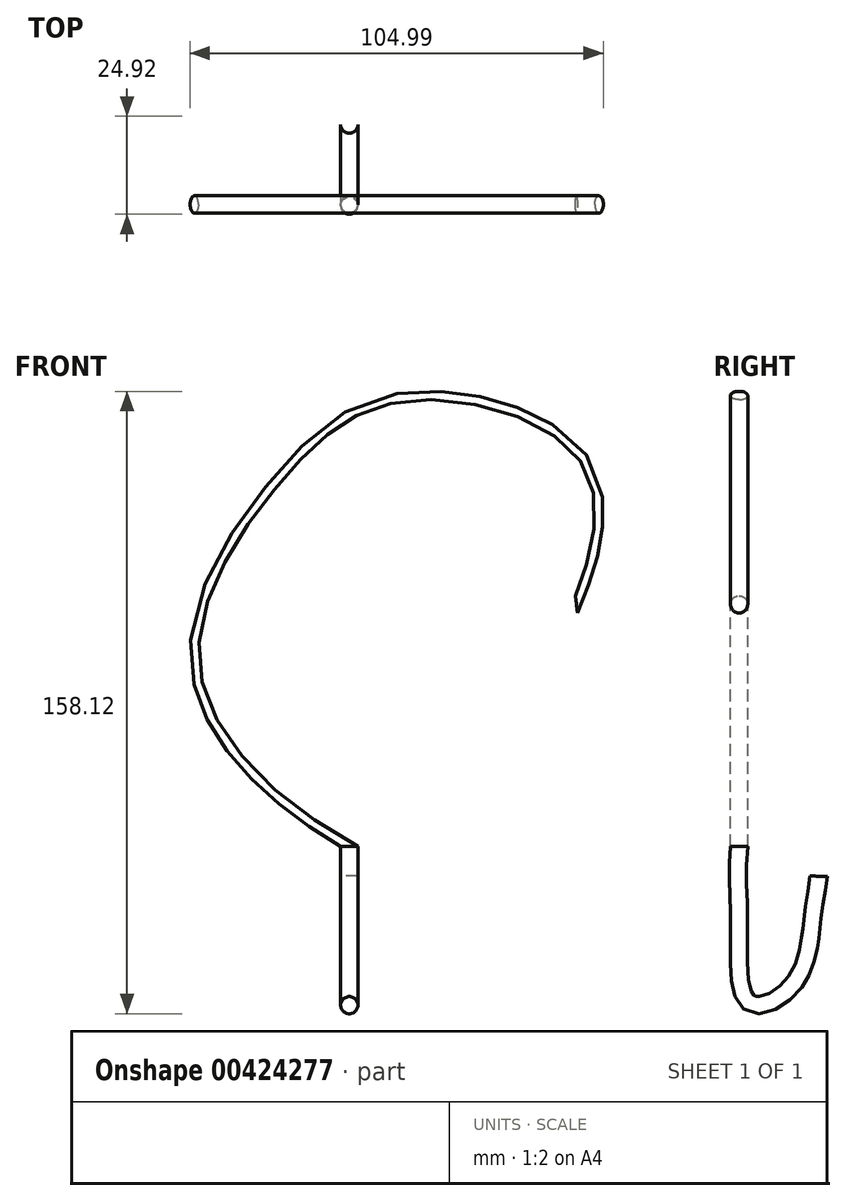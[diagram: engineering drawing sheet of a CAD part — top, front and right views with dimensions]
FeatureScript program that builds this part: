
annotation { "Feature Type Name" : "Feature", "Feature Type Description" : "" }
export const myFeature = defineFeature(function(context is Context, id is Id, definition is map)
    precondition{}
    {
        {
            var Q0;
            Q0=qCreatedBy(makeId("Front.planeOp"),FACE);
            var sketch = newSketch(context, id + "F0", { "sketchPlane" : qUnion([Q0])});
            skFitSpline(sketch, "E0", {"points": [v(0, 0) * mm, v(-39.16, 45.8) * mm, v(-18.04, 93.51) * mm, v(15.1, 114.27) * mm, v(60.62, 96.79) * mm, v(57.7, 61.46) * mm], "startDerivative": vector(-260.8, 144.56) * mm, "endDerivative": vector(-67.27, -161.45) * mm});
            skSolve(sketch);
        }
        {
            var Q0;
            Q0=qCreatedBy(makeId("Top.planeOp"),FACE);
            var sketch = newSketch(context, id + "F1", { "sketchPlane" : qUnion([Q0])});
            skCircle(sketch, "E1", {"center": v(0, 0) * mm, "radius": 2.19 * mm});
            skSolve(sketch);
        }
        {
            var Q0;
            Q0 = qSketchRegion(id + "F1", true);
            var Q1;
            Q1 = qConstructionFilter(qBodyType(qCreatedBy(id + "F0" ,EDGE), BodyType.WIRE), ConstructionObject.NO);
            sweep(context, id + "F2", {"profiles" : qUnion([Q0]), "path" : qUnion([Q1])});
        }
        {
            var Q0;
            Q0=qCreatedBy(makeId("Right.planeOp"),FACE);
            var sketch = newSketch(context, id + "F3", { "sketchPlane" : qUnion([Q0])});
            skFitSpline(sketch, "E2", {"points": [v(0, 0) * mm, v(0, -19.9) * mm, v(2.74, -39.78) * mm, v(13.99, -34.78) * mm, v(18.36, -20.73) * mm, v(20.23, -7.6) * mm], "startDerivative": vector(-9.76, -83.72) * mm, "endDerivative": vector(20.52, 133.36) * mm});
            skSolve(sketch);
        }
        {
            var Q0;
            Q0 = qSketchRegion(id + "F1", true);
            var Q1;
            Q1 = qConstructionFilter(qBodyType(qCreatedBy(id + "F3" ,EDGE), BodyType.WIRE), ConstructionObject.NO);
            sweep(context, id + "F4", {"operationType" : NewBodyOperationType.ADD, "profiles" : qUnion([Q0]), "path" : qUnion([Q1])});
        }
    });
